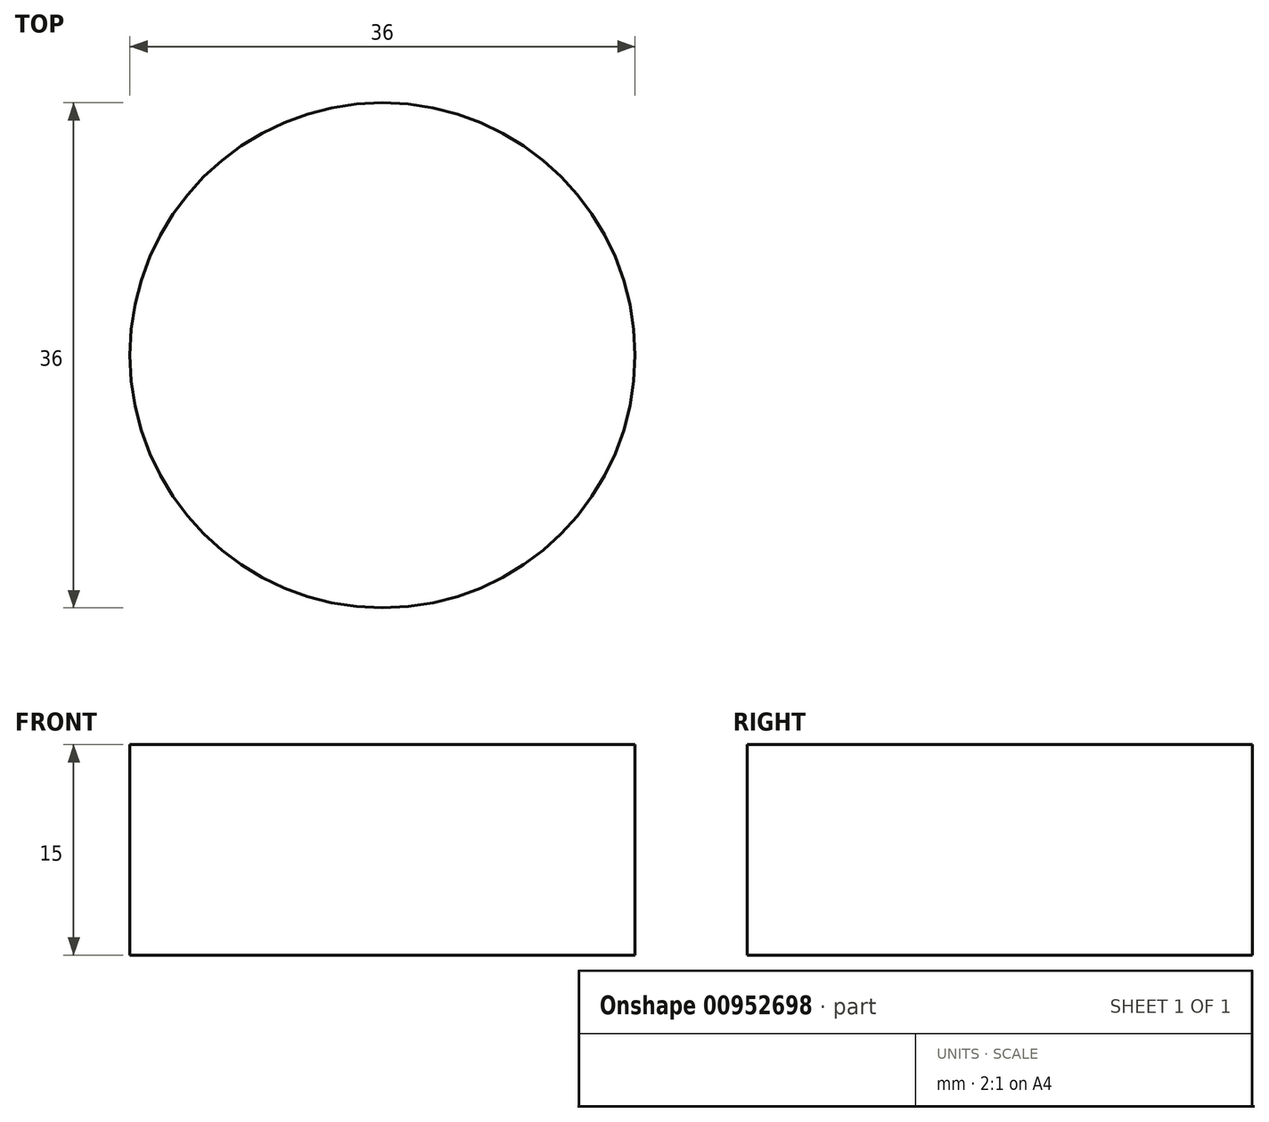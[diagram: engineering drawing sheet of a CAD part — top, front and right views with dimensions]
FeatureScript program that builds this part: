
annotation { "Feature Type Name" : "Feature", "Feature Type Description" : "" }
export const myFeature = defineFeature(function(context is Context, id is Id, definition is map)
    precondition{}
    {
        {
            var Q0;
            Q0=qCreatedBy(makeId("Top.planeOp"),FACE);
            var sketch = newSketch(context, id + "F0", { "sketchPlane" : qUnion([Q0])});
            skCircle(sketch, "E0", {"center": v(0, 0) * mm, "radius": 18 * mm});
            skSolve(sketch);
        }
        {
            var Q0;
            Q0=makeQuery(id+"F0.imprint","IMPRINT",FACE,{"disambiguationData":[TD([[makeQuery(id+"F0.imprint","IMPRINT",EDGE,{"derivedFrom":sQuery(id+"F0.wireOp",EDGE,"E0")}),1.0]])]});
            extrude(context, id + "F1", {"entities" : qUnion([Q0]), "depth" : 15 * mm, "offsetDistance" : 25 * mm});
        }
    });
